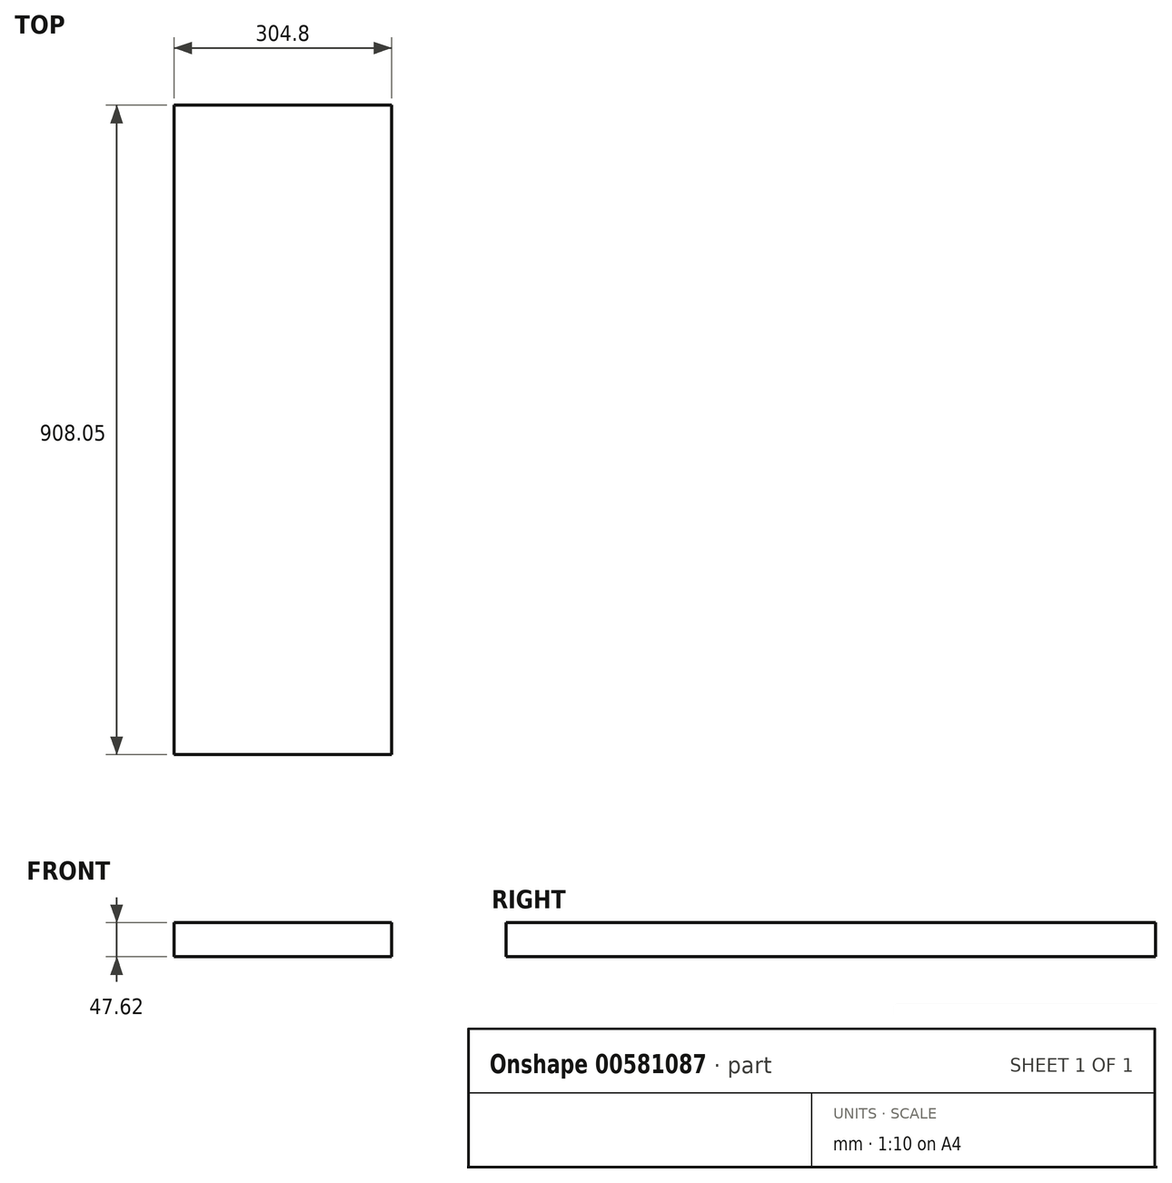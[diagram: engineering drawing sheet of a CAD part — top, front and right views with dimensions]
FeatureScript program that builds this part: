
annotation { "Feature Type Name" : "Feature", "Feature Type Description" : "" }
export const myFeature = defineFeature(function(context is Context, id is Id, definition is map)
    precondition{}
    {
        {
            var Q0;
            Q0=qCreatedBy(makeId("Front.planeOp"),FACE);
            var sketch = newSketch(context, id + "F0", { "sketchPlane" : qUnion([Q0])});
            skLineSegment(sketch, "E0.bottom", {"start": v(152.4, 23.81) * mm, "end": v(-152.4, 23.81) * mm});
            skLineSegment(sketch, "E0.top", {"start": v(152.4, -23.81) * mm, "end": v(-152.4, -23.81) * mm});
            skLineSegment(sketch, "E0.left", {"start": v(152.4, 23.81) * mm, "end": v(152.4, -23.81) * mm});
            skLineSegment(sketch, "E0.right", {"start": v(-152.4, 23.81) * mm, "end": v(-152.4, -23.81) * mm});
            skPoint(sketch, "E0.middle", {"position": v(0, 0) * mm});
            skSolve(sketch);
        }
        {
            var Q0;
            Q0=makeQuery(id+"F0.imprint","IMPRINT",FACE,{"disambiguationData":[TD([[makeQuery(id+"F0.imprint","IMPRINT",EDGE,{"derivedFrom":sQuery(id+"F0.wireOp",EDGE,"E0.bottom")}),1.0]])]});
            extrude(context, id + "F1", {"entities" : qUnion([Q0]), "depth" : 908.05 * mm, "offsetDistance" : 25.4 * mm});
        }
    });
